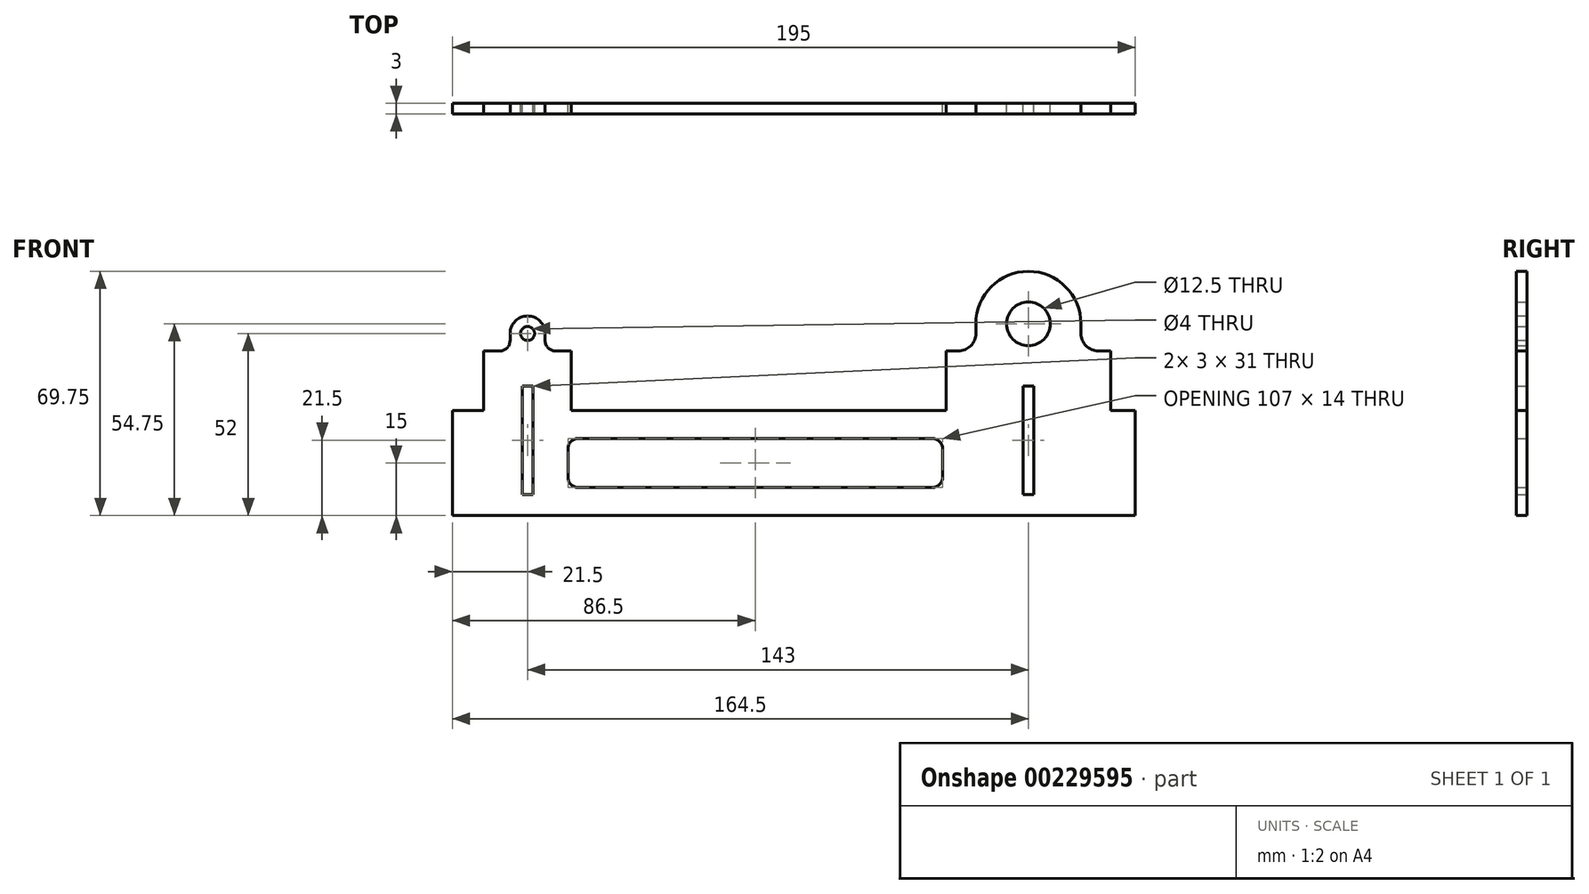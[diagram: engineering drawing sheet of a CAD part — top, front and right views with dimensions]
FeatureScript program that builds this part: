
annotation { "Feature Type Name" : "Feature", "Feature Type Description" : "" }
export const myFeature = defineFeature(function(context is Context, id is Id, definition is map)
    precondition{}
    {
        {
            var Q0;
            Q0=qCreatedBy(makeId("Front.planeOp"),FACE);
            var sketch = newSketch(context, id + "F0", { "sketchPlane" : qUnion([Q0])});
            skLineSegment(sketch, "E0.bottom", {"start": v(97.5, -15) * mm, "end": v(-97.5, -15) * mm});
            skLineSegment(sketch, "E0.top", {"start": v(97.5, 15) * mm, "end": v(90.5, 15) * mm});
            skLineSegment(sketch, "E0.left", {"start": v(97.5, -15) * mm, "end": v(97.5, 15) * mm});
            skLineSegment(sketch, "E0.right", {"start": v(-97.5, -15) * mm, "end": v(-97.5, 15) * mm});
            skPoint(sketch, "E0.middle", {"position": v(0, 0) * mm});
            skLineSegment(sketch, "E1.top", {"start": v(-88.5, 32) * mm, "end": v(-84, 32) * mm});
            skLineSegment(sketch, "E1.left", {"start": v(-88.5, 15) * mm, "end": v(-88.5, 32) * mm});
            skLineSegment(sketch, "E1.right", {"start": v(-63.5, 15) * mm, "end": v(-63.5, 32) * mm});
            skLineSegment(sketch, "E2.bottom", {"start": v(-61.5, 7) * mm, "end": v(39.5, 7) * mm});
            skLineSegment(sketch, "E2.top", {"start": v(-61.5, -7) * mm, "end": v(39.5, -7) * mm});
            skLineSegment(sketch, "E2.left", {"start": v(-64.5, 4) * mm, "end": v(-64.5, -4) * mm});
            skLineSegment(sketch, "E2.right", {"start": v(42.5, 4) * mm, "end": v(42.5, -4) * mm});
            skLineSegment(sketch, "E3.top", {"start": v(43.5, 32) * mm, "end": v(47, 32) * mm});
            skLineSegment(sketch, "E3.left", {"start": v(43.5, 15) * mm, "end": v(43.5, 32) * mm});
            skLineSegment(sketch, "E3.right", {"start": v(90.5, 15) * mm, "end": v(90.5, 32) * mm});
            skArc(sketch, "E4", {"start": v(82, 39.75) * mm, "mid": v(67, 54.75) * mm, "end": v(52, 39.75) * mm});
            skCircle(sketch, "E5", {"center": v(67, 39.75) * mm, "radius": 6.25 * mm});
            skLineSegment(sketch, "E6", {"start": v(52, 39.75) * mm, "end": v(52, 37) * mm});
            skLineSegment(sketch, "E7", {"start": v(82, 39.75) * mm, "end": v(82, 37) * mm});
            skLineSegment(sketch, "E8.trimOffspring", {"start": v(87, 32) * mm, "end": v(90.5, 32) * mm});
            skPoint(sketch, "E9.visualSharp", {"position": v(52, 32) * mm});
            skArc(sketch, "E9.filletArc", {"start": v(47, 32) * mm, "mid": v(50.54, 33.46) * mm, "end": v(52, 37) * mm});
            skPoint(sketch, "E10.visualSharp", {"position": v(82, 32) * mm});
            skArc(sketch, "E10.filletArc", {"start": v(82, 37) * mm, "mid": v(83.46, 33.46) * mm, "end": v(87, 32) * mm});
            skArc(sketch, "E11", {"start": v(-71, 37) * mm, "mid": v(-76, 42) * mm, "end": v(-81, 37) * mm});
            skCircle(sketch, "E12", {"center": v(-76, 37) * mm, "radius": 2 * mm});
            skLineSegment(sketch, "E13", {"start": v(-81, 37) * mm, "end": v(-81, 35) * mm});
            skLineSegment(sketch, "E14", {"start": v(-71, 37) * mm, "end": v(-71, 35) * mm});
            skLineSegment(sketch, "E15.trimOffspring", {"start": v(-68, 32) * mm, "end": v(-63.5, 32) * mm});
            skPoint(sketch, "E16.visualSharp", {"position": v(-81, 32) * mm});
            skArc(sketch, "E16.filletArc", {"start": v(-84, 32) * mm, "mid": v(-81.88, 32.88) * mm, "end": v(-81, 35) * mm});
            skPoint(sketch, "E17.visualSharp", {"position": v(-71, 32) * mm});
            skArc(sketch, "E17.filletArc", {"start": v(-71, 35) * mm, "mid": v(-70.12, 32.88) * mm, "end": v(-68, 32) * mm});
            skLineSegment(sketch, "E18.trimOffspring", {"start": v(-88.5, 15) * mm, "end": v(-97.5, 15) * mm});
            skLineSegment(sketch, "E19.trimOffspring", {"start": v(43.5, 15) * mm, "end": v(-63.5, 15) * mm});
            skPoint(sketch, "E20.visualSharp", {"position": v(-64.5, 7) * mm});
            skArc(sketch, "E20.filletArc", {"start": v(-61.5, 7) * mm, "mid": v(-63.62, 6.12) * mm, "end": v(-64.5, 4) * mm});
            skPoint(sketch, "E21.visualSharp", {"position": v(-64.5, -7) * mm});
            skArc(sketch, "E21.filletArc", {"start": v(-64.5, -4) * mm, "mid": v(-63.62, -6.12) * mm, "end": v(-61.5, -7) * mm});
            skPoint(sketch, "E22.visualSharp", {"position": v(42.5, 7) * mm});
            skArc(sketch, "E22.filletArc", {"start": v(42.5, 4) * mm, "mid": v(41.62, 6.12) * mm, "end": v(39.5, 7) * mm});
            skPoint(sketch, "E23.visualSharp", {"position": v(42.5, -7) * mm});
            skArc(sketch, "E23.filletArc", {"start": v(39.5, -7) * mm, "mid": v(41.62, -6.12) * mm, "end": v(42.5, -4) * mm});
            skLineSegment(sketch, "E24.bottom", {"start": v(-74.5, -9) * mm, "end": v(-77.5, -9) * mm});
            skLineSegment(sketch, "E24.top", {"start": v(-74.5, 22) * mm, "end": v(-77.5, 22) * mm});
            skLineSegment(sketch, "E24.left", {"start": v(-74.5, -9) * mm, "end": v(-74.5, 22) * mm});
            skLineSegment(sketch, "E24.right", {"start": v(-77.5, -9) * mm, "end": v(-77.5, 22) * mm});
            skPoint(sketch, "E24.middle", {"position": v(-76, 6.5) * mm});
            skLineSegment(sketch, "E25.bottom", {"start": v(68.5, -9) * mm, "end": v(65.5, -9) * mm});
            skLineSegment(sketch, "E25.top", {"start": v(68.5, 22) * mm, "end": v(65.5, 22) * mm});
            skLineSegment(sketch, "E25.left", {"start": v(68.5, -9) * mm, "end": v(68.5, 22) * mm});
            skLineSegment(sketch, "E25.right", {"start": v(65.5, -9) * mm, "end": v(65.5, 22) * mm});
            skPoint(sketch, "E25.middle", {"position": v(67, 6.5) * mm});
            skSolve(sketch);
        }
        {
            var Q0;
            Q0=makeQuery(id+"F0.imprint","IMPRINT",FACE,{"disambiguationData":[TD([[makeQuery(id+"F0.imprint","IMPRINT",EDGE,{"derivedFrom":sQuery(id+"F0.wireOp",EDGE,"E0.bottom")}),-1.0]])]});
            extrude(context, id + "F1", {"entities" : qUnion([Q0]), "depth" : 3 * mm});
        }
    });
